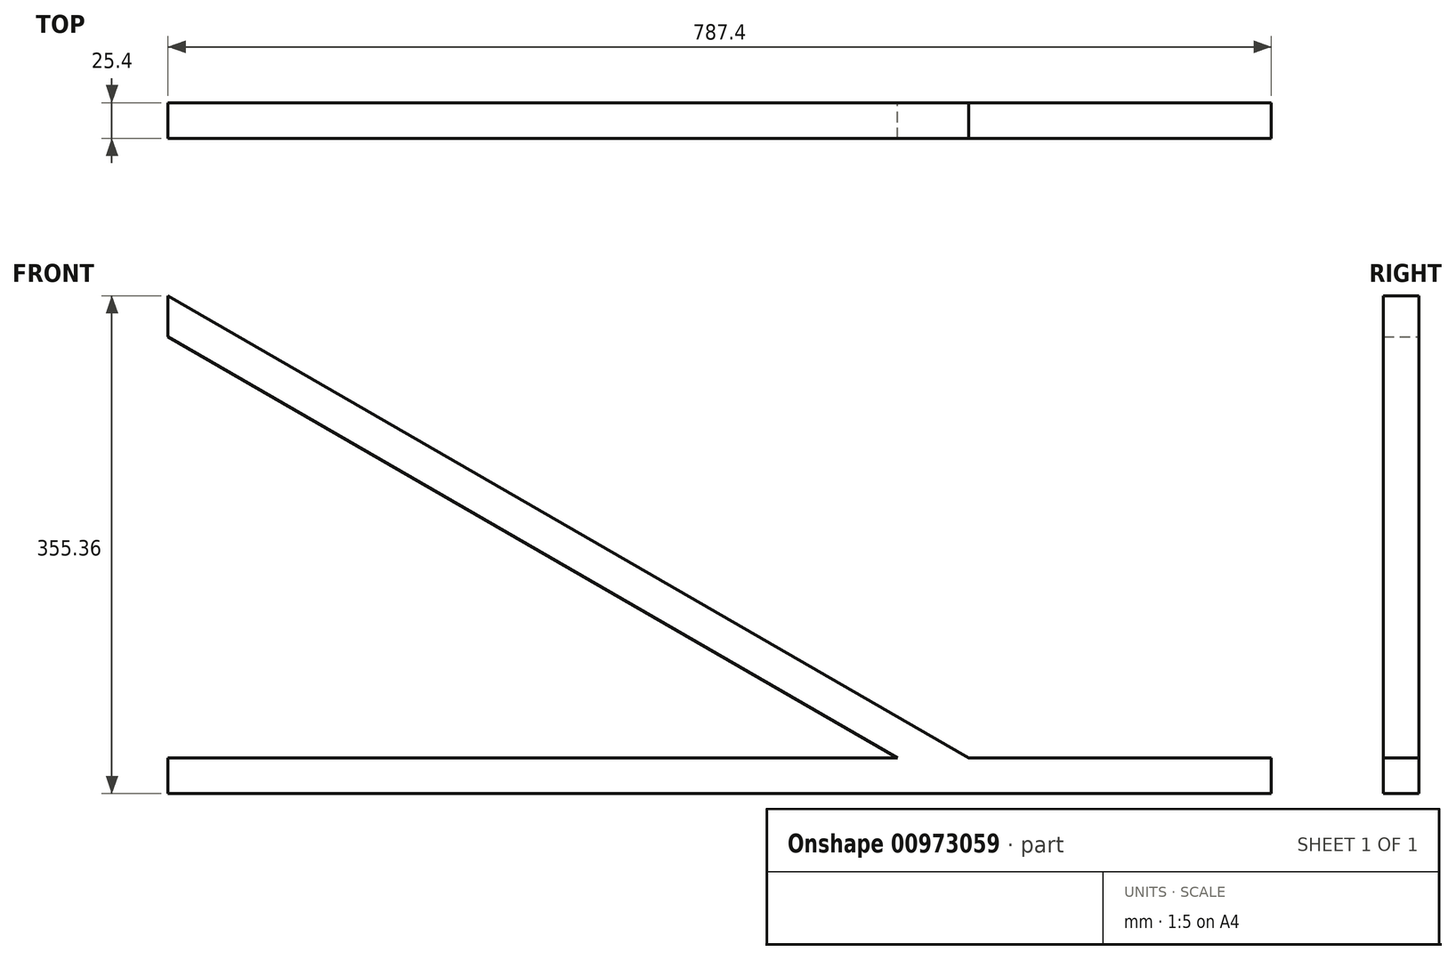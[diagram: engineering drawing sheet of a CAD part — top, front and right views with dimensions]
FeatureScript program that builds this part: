
annotation { "Feature Type Name" : "Feature", "Feature Type Description" : "" }
export const myFeature = defineFeature(function(context is Context, id is Id, definition is map)
    precondition{}
    {
        {
            var Q0;
            Q0=qCreatedBy(makeId("Front.planeOp"),FACE);
            var sketch = newSketch(context, id + "F0", { "sketchPlane" : qUnion([Q0])});
            skLineSegment(sketch, "E0.bottom", {"start": v(0, 0) * mm, "end": v(787.4, 0) * mm});
            skLineSegment(sketch, "E0.top", {"start": v(0, 25.4) * mm, "end": v(520.7, 25.4) * mm});
            skLineSegment(sketch, "E0.left", {"start": v(0, 0) * mm, "end": v(0, 25.4) * mm});
            skLineSegment(sketch, "E0.right", {"start": v(787.4, 0) * mm, "end": v(787.4, 25.4) * mm});
            skLineSegment(sketch, "E1", {"start": v(520.7, 25.4) * mm, "end": v(0, 326.03) * mm});
            skLineSegment(sketch, "E2", {"start": v(0, 326.03) * mm, "end": v(0, 355.36) * mm});
            skLineSegment(sketch, "E3", {"start": v(0, 355.36) * mm, "end": v(571.5, 25.4) * mm});
            skLineSegment(sketch, "E4.trimOffspring", {"start": v(571.5, 25.4) * mm, "end": v(787.4, 25.4) * mm});
            skSolve(sketch);
        }
        {
            var Q0;
            Q0=makeQuery(id+"F0.imprint","IMPRINT",FACE,{"disambiguationData":[TD([[makeQuery(id+"F0.imprint","IMPRINT",EDGE,{"derivedFrom":sQuery(id+"F0.wireOp",EDGE,"E0.bottom")}),1.0]])]});
            extrude(context, id + "F1", {"entities" : qUnion([Q0]), "depth" : 25.4 * mm, "offsetDistance" : 25.4 * mm});
        }
    });
